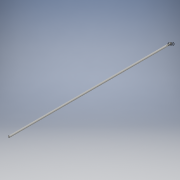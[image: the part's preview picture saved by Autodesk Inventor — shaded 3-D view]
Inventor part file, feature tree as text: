
AUTODESK INVENTOR PART (.ipt)
format: ipt  version: 2016 (Build 200138000, 138)  size: 89,088 bytes
history: native  units: in
note: dims shown in document units (in); Inventor stores cm internally (conversion verified against a paired STEP export)
features: sketch x2, extrude x1
ambient origin geometry x8: Origin, YZ Plane, XZ Plane, XY Plane, X Axis, Y Axis, Z Axis, Center Point
bodies: Solid1 (feature_tree)
feature tree (3):
  extrude  "Extrusion1"  Depth=48.0in
  sketch  "Sketch2"  dims[d5=0.6in]
  sketch  "Sketch1"  dims[d1=48.0in d2=0.0in d4=0.5in]
